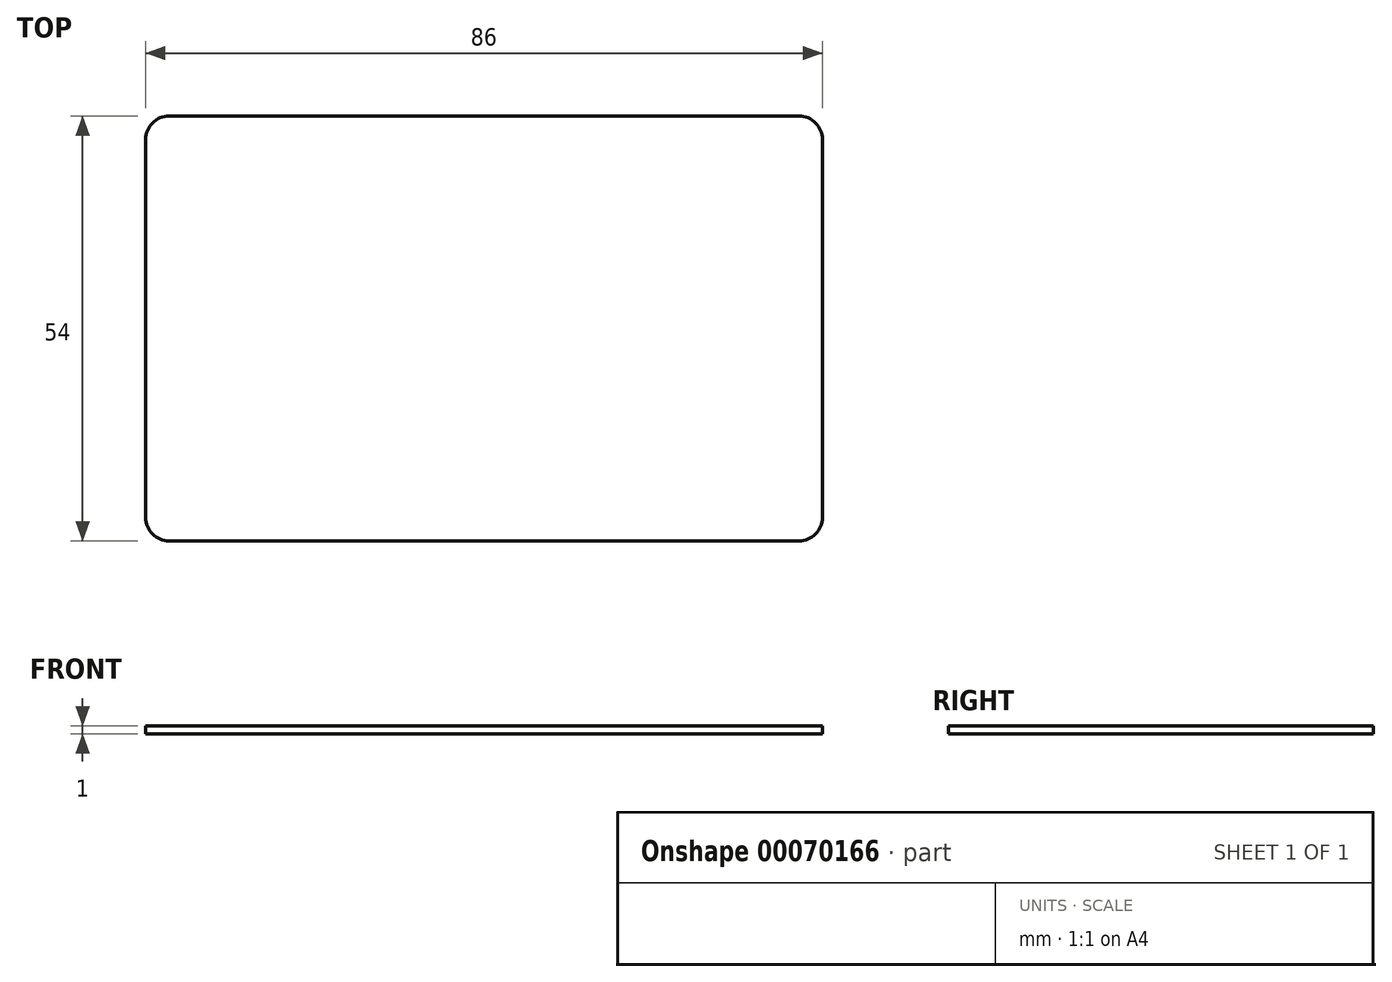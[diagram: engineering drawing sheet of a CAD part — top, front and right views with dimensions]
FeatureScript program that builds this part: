
annotation { "Feature Type Name" : "Feature", "Feature Type Description" : "" }
export const myFeature = defineFeature(function(context is Context, id is Id, definition is map)
    precondition{}
    {
        {
            var Q0;
            Q0=qCreatedBy(makeId("Top.planeOp"),FACE);
            var sketch = newSketch(context, id + "F0", { "sketchPlane" : qUnion([Q0])});
            skLineSegment(sketch, "E0.rect.bottom", {"start": v(40, -27) * mm, "end": v(-40, -27) * mm});
            skLineSegment(sketch, "E0.rect.top", {"start": v(40, 27) * mm, "end": v(-40, 27) * mm});
            skLineSegment(sketch, "E0.rect.left", {"start": v(43, -24) * mm, "end": v(43, 24) * mm});
            skLineSegment(sketch, "E0.rect.right", {"start": v(-43, -24) * mm, "end": v(-43, 24) * mm});
            skPoint(sketch, "E0.rect.middle", {"position": v(0, 0) * mm});
            skPoint(sketch, "E1.visualSharp", {"position": v(43, 27) * mm});
            skArc(sketch, "E1.filletArc", {"start": v(43, 24) * mm, "mid": v(42.12, 26.12) * mm, "end": v(40, 27) * mm});
            skPoint(sketch, "E2.visualSharp", {"position": v(43, -27) * mm});
            skArc(sketch, "E2.filletArc", {"start": v(40, -27) * mm, "mid": v(42.12, -26.12) * mm, "end": v(43, -24) * mm});
            skPoint(sketch, "E3.visualSharp", {"position": v(-43, 27) * mm});
            skArc(sketch, "E3.filletArc", {"start": v(-40, 27) * mm, "mid": v(-42.12, 26.12) * mm, "end": v(-43, 24) * mm});
            skPoint(sketch, "E4.visualSharp", {"position": v(-43, -27) * mm});
            skArc(sketch, "E4.filletArc", {"start": v(-43, -24) * mm, "mid": v(-42.12, -26.12) * mm, "end": v(-40, -27) * mm});
            skSolve(sketch);
        }
        {
            var Q0;
            Q0=makeQuery(id+"F0.imprint","IMPRINT",FACE,{"disambiguationData":[TD([[makeQuery(id+"F0.imprint","IMPRINT",EDGE,{"derivedFrom":sQuery(id+"F0.wireOp",EDGE,"E0.rect.bottom")}),-1.0]])]});
            extrude(context, id + "F1", {"entities" : qUnion([Q0]), "depth" : 1 * mm});
        }
    });
